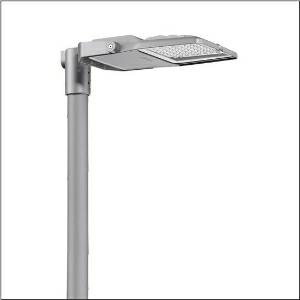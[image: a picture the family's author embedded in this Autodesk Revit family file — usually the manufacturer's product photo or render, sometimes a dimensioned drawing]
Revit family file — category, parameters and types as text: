
# Revit family: floodlight_fl_21_iq_mini___pl52_5xa7772d2d3a_9966
name_source: partatom
category: Lighting Fixtures
units: mm (PartAtom-declared; Revit-internal decimal feet)

## family parameters
Cut with Voids When Loaded = No
Host = Face
Light Source = No
Part Type = Normal
Room Calculation Point = No
Round Connector Dimension = Use Diameter
Shared = No

## types (1)
- --- (1 x LED, 17830 lm, 143 W, 3000K)
    Apparent Load = 143 VA
    CIE Flux Codes = 26 60 98 100 100
    Color Rendering = 70
    Color Temperature = 3000K
    Default Elevation = 1800 mm
    Description = Floodlight FL 21 iQ mini, floodlight, primary light control with lens, of PMMA, primary optical cover: protective disc, of toughened safety glass, transparent, light distribution: PL52, light emission: direct distribution, installation type: surface-mounted, LED, High Power LED, rated luminous flux: 17.830lm, luminous efficacy: 125lm/W, light colour: 730, colour temperature: 3000K, control gear: iQ Street-Remote/DALI, control: Auto-Match, Temp-Guard, Night-Set, Smart-Wire, Desk-Remote (wireless, voltage-free reading and setting of iQ features in the workshop via application-optimized NFC function/RFID function), optimised constant luminous flux control (CLO 2.0), Light-Fading, Lumen-Switch, with terminal, 6-pole, mains connection: 220..240V, AC, 50/60Hz, start of lifetime: 143W, end of service life: 152W, reduction: 61W, luminaire housing, of diecast aluminium, powder-coated, Siteco® metallic grey (DB 702S), corrosivity category C5 mid according to DIN EN ISO 12944, suitable for swimming pools, chlorine-resistant, sealing non-destructively replaceable, please order mast flange separately, mast bracket, of steel, galvanised, powder-coated, protection rating (complete): IP66, insulation class (complete): insulation class II (safety insulation), certification: CE, ENEC, VDE, protection symbol: D, impact resistance: IK08, permissible operating ambient temperature: -40..+40°C, permissible operating ambient temperature for outdoor applications: -40..+50°C, standard: DIN EN 12944, LABS conformity tested according to VDMA 24364:2018-05, packaging unit: 1 piece

Light Distribution: PL52
    Height = 70 mm
    Lamp = 1 x LED
    Lamp Light Flux = 17830 lm
    Lamp Power = 143 W
    Lamp count = 1
    Length = 485 mm
    Luminous efficacy = 125 lm/W
    Manufacturer = Siteco
    ModVariant = No
    Model = 5XA7772D2D3A
    Number of Poles = 1
    OnlyDefault = Yes
    Power Factor = 1
    Product Name = Floodlight FL 21 iQ mini | PL52
    Product group = floodlight | pylon annexe
    ProductGroupID = 6200
    Protection Class = Protection class II
    Protection Degree = IP 66
    RLX_Detail_Level = 1
    RLX_Emergency_Light_Flux = 0 lm
    RLX_Emergency_Type = 0
    RLX_Emergency_Type_DB = No
    RlxData = <blob elided: 101841 chars, md5=ad8b5fce>
    Socket = socket
    Standby Power = 0 W
    System Light Flux = 17830 lm
    System Power = 143 W
    Type Comments = factory setting: luminous flux: 100 % | dim-lin: 254 | 730 mA
    Type Image = l_1007125.jpg
    URL = http://relux.com
    VarID = @adj_163712
    Voltage = 0 V
    Weight = 0.00 kg
    Width = 337 mm

## geometry (parser evidence)
native form markers: Blend x4, Sweep x11
no freeform markers — native parametric forms only
